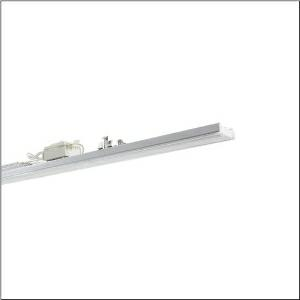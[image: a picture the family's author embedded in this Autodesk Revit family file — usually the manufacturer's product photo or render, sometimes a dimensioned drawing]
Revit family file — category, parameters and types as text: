
# Revit family: licross_21_recessed_mo_52tl1ede445g
name_source: partatom
category: Lighting Fixtures
units: mm (PartAtom-declared; Revit-internal decimal feet)

## family parameters
Cut with Voids When Loaded = No
Host = Face
Light Source = No
Part Type = Normal
Room Calculation Point = No
Round Connector Dimension = Use Diameter
Shared = No

## types (1)
- --- (1 x LED, 4970 lm, 29.9 W, 4000K)
    Apparent Load = 30 VA
    CIE Flux Codes = 85 95 99 100 100
    Color Rendering = 80
    Color Temperature = 4000K
    Default Elevation = 1800 mm
    Description = Licross 21 Recessed MO, luminaire insert, of sheet steel, galvanised, coil coated, white, length: 750mm, width: 66mm, height: 67mm, LED rated luminous flux: 4.970lm, light colour: 840, SDCM (Standard Deviation of Colour Matching)MacAdam ≤ 3 SDCM (initial), control gear: DALI 2, with plug, 5-pole, with phase selection, mains connection: 220..240V, AC, 50/60Hz, rated input power: 30W, internal wiring halogen-free, primary light control with lens, of plastic, primary optical cover: cover, of PMMA, light emission: direct distribution, primary light characteristic: symmetric, protection rating (complete): IP40, insulation class (complete): insulation class I (protective earthing), certification: CE, ENEC, VDE, UKCA, protection symbol: D if used in an environment without relevant dust loads with corresponding accessories, impact resistance: IK06, permissible ambient temperature for indoor applications: -25..+35°C, corresponds to IFS (International Featured Standards) requirements for safety and quality in the food industry, reducing of maximum allowable ambient temperature of 5°C with ceiling mounting, LABS conformity tested according to VDMA 24364:2018-05, The light source and the operating device comply with the requirements of the Ecodesign Regulation (EU) 2019/2020 and are replaceable in accordance with this regulation, packaging unit: 1 piece
    Height = 58 mm
    Lamp = 1 x LED
    Lamp Light Flux = 4970 lm
    Lamp Power = 29.9 W
    Lamp count = 1
    Length = 750 mm
    Luminous efficacy = 166 lm/W
    Manufacturer = Siteco
    ModVariant = No
    Model = 52TL1EDE445G
    Mounting Place = Ceiling
    Mounting Type = Pendant
    Number of Poles = 1
    OnlyDefault = Yes
    Power Factor = 1
    Product Name = Licross 21 Recessed MO
    Product group = luminaire insert | ceiling pendant
    ProductGroupID = 901
    Protection Class = Protection class I
    Protection Degree = IP 40
    RLX_Detail_Level = 1
    RLX_Emergency_Light_Flux = 0 lm
    RLX_Emergency_Type = 0
    RLX_Emergency_Type_DB = No
    RlxData = <blob elided: 29281 chars, md5=0eddd8cd>
    Socket = socket
    Standby Power = 0 W
    System Light Flux = 4970 lm
    System Power = 30 W
    Type Comments = factory setting: luminous flux: 100 % | dim-lin: 254 | 390 mA
    Type Image = l_1296930.jpg
    URL = http://relux.com
    VarID = @adj_125841
    Voltage = 0 V
    Weight = 0.00 kg
    Width = 66 mm

## geometry (parser evidence)
native form markers: Blend x4, Sweep x12
no freeform markers — native parametric forms only
